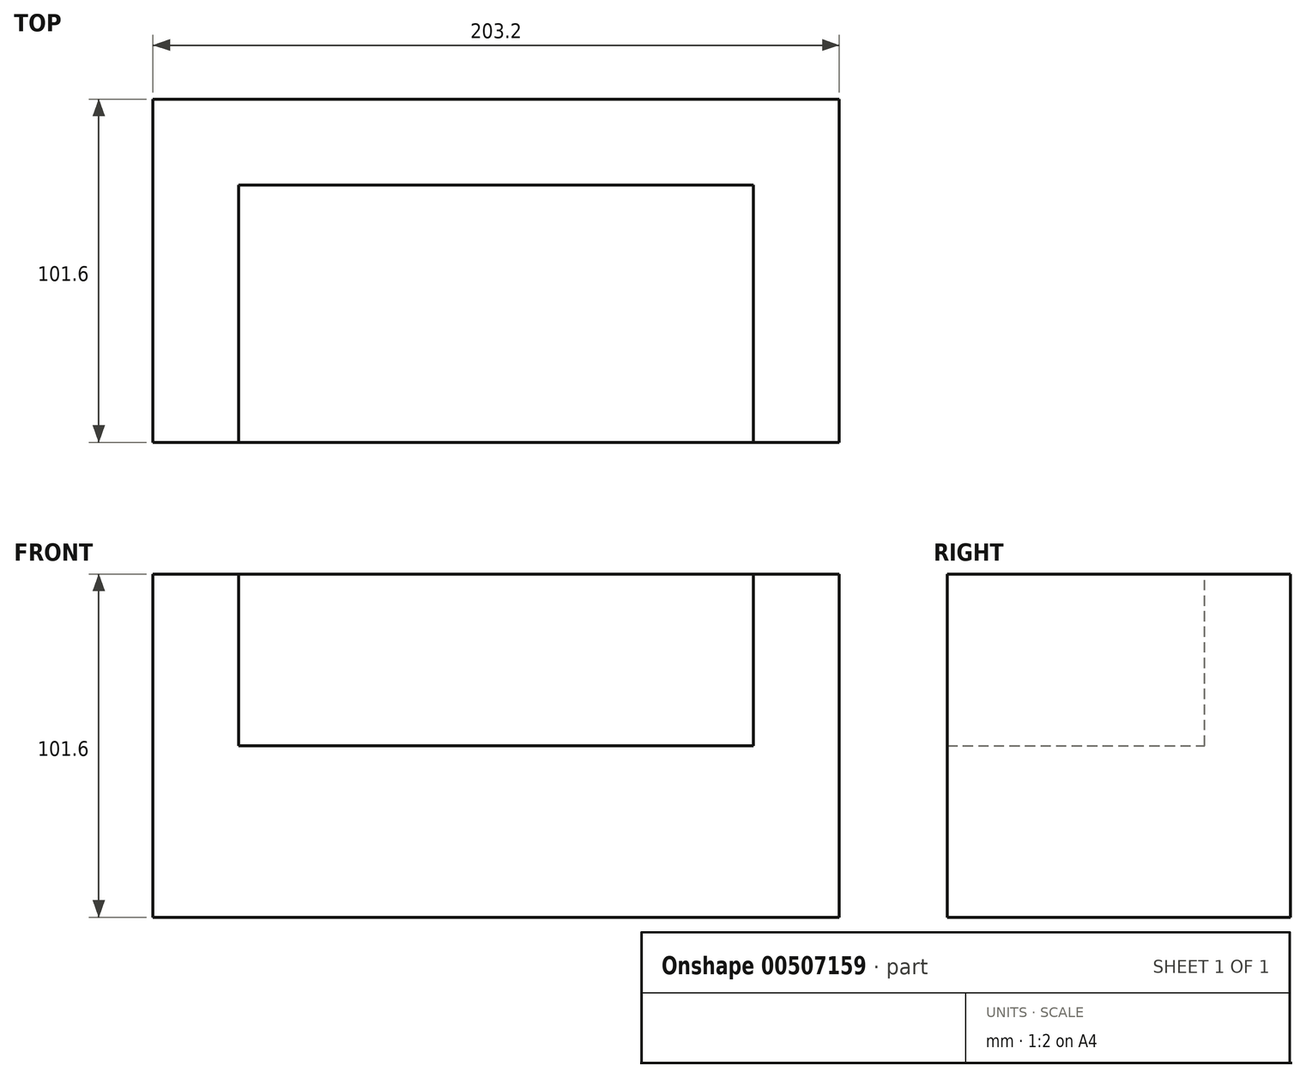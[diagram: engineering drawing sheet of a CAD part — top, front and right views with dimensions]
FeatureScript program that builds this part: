
annotation { "Feature Type Name" : "Feature", "Feature Type Description" : "" }
export const myFeature = defineFeature(function(context is Context, id is Id, definition is map)
    precondition{}
    {
        {
            var Q0;
            Q0=qCreatedBy(makeId("Top.planeOp"),FACE);
            var sketch = newSketch(context, id + "F0", { "sketchPlane" : qUnion([Q0])});
            skLineSegment(sketch, "E0", {"start": v(-66.42, 58.92) * mm, "end": v(-66.42, -42.68) * mm});
            skLineSegment(sketch, "E1", {"start": v(-66.42, -42.68) * mm, "end": v(136.78, -42.68) * mm});
            skLineSegment(sketch, "E2", {"start": v(136.78, -42.68) * mm, "end": v(136.78, 58.92) * mm});
            skLineSegment(sketch, "E3", {"start": v(136.78, 58.92) * mm, "end": v(-66.42, 58.92) * mm});
            skSolve(sketch);
        }
        {
            var Q0;
            Q0 = qSketchRegion(id + "F0", true);
            extrude(context, id + "F1", {"entities" : qUnion([Q0]), "depth" : 101.6 * mm});
        }
        {
            var Q0;
            Q0=makeQuery(id+"F1.opExtrude","CAP_FACE",FACE,{"disambiguationData":[OSD([sQuery(id+"F0.wireOp",EDGE,"E0"),sQuery(id+"F0.wireOp",EDGE,"E1"),sQuery(id+"F0.wireOp",EDGE,"E2"),sQuery(id+"F0.wireOp",EDGE,"E3")])],"isStart":false});
            var sketch = newSketch(context, id + "F2", { "sketchPlane" : qUnion([Q0])});
            skLineSegment(sketch, "E4", {"start": v(-41.02, -42.68) * mm, "end": v(-41.02, 33.52) * mm});
            skLineSegment(sketch, "E5", {"start": v(-41.02, 33.52) * mm, "end": v(111.38, 33.52) * mm});
            skLineSegment(sketch, "E6", {"start": v(111.38, 33.52) * mm, "end": v(111.38, -42.68) * mm});
            skSolve(sketch);
        }
        {
            var Q0;
            Q0 = qSketchRegion(id + "F2", true);
            var Q1;
            {var subQ0=sQuery(id+"F2.wireOp",EDGE,"E4");Q1=makeQuery(id+"F2.imprint","IMPRINT",FACE,{"disambiguationData":[TD([[makeQuery(id+"F2.imprint","IMPRINT",EDGE,{"derivedFrom":subQ0}),-1.0]])]});}
            extrude(context, id + "F3", {"entities" : qUnion([Q0, Q1]), "operationType" : NewBodyOperationType.REMOVE, "oppositeDirection" : true, "depth" : 50.8 * mm});
        }
    });
